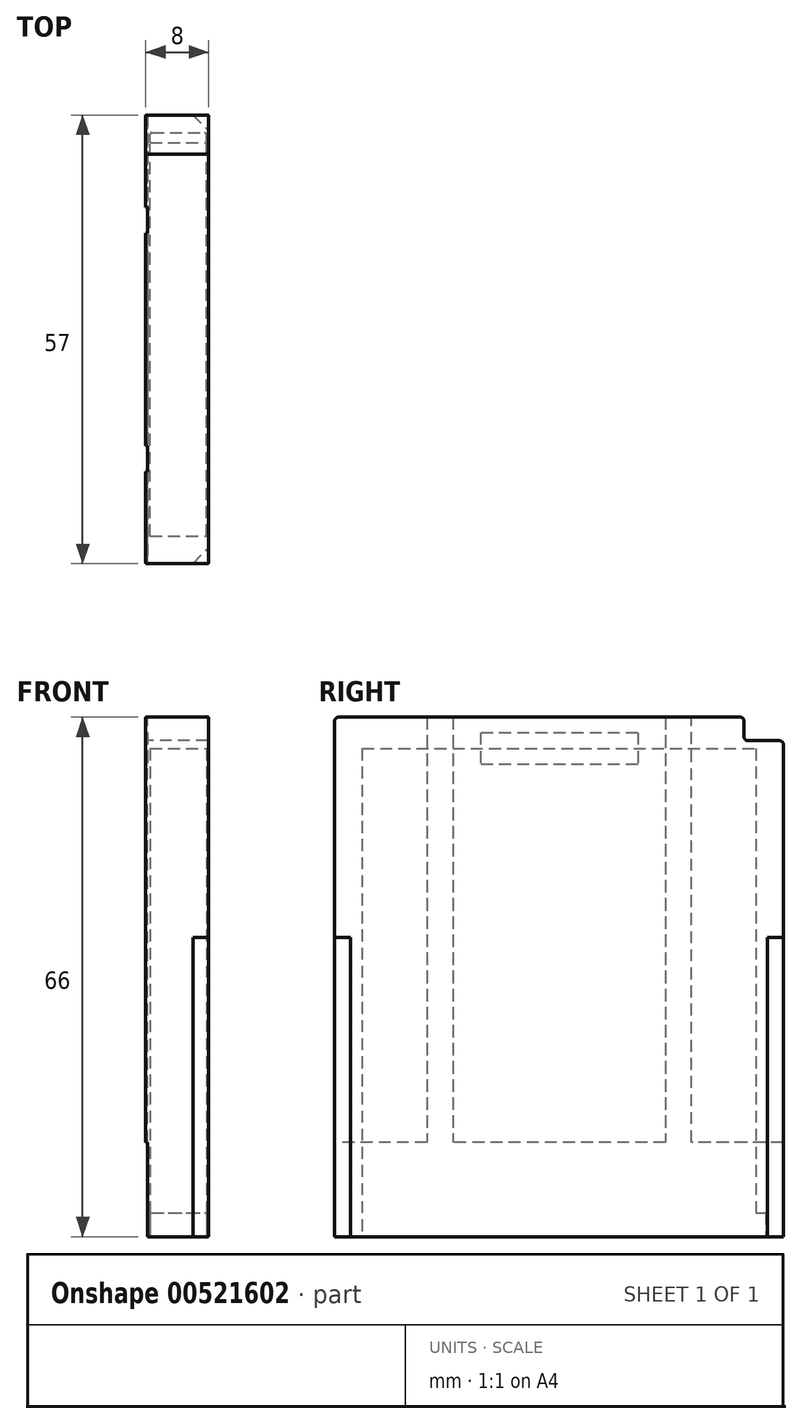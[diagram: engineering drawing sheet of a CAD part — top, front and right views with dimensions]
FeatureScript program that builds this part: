
annotation { "Feature Type Name" : "Feature", "Feature Type Description" : "" }
export const myFeature = defineFeature(function(context is Context, id is Id, definition is map)
    precondition{}
    {
        {
            var Q0;
            Q0=qCreatedBy(makeId("Right.planeOp"),FACE);
            var sketch = newSketch(context, id + "F0", { "sketchPlane" : qUnion([Q0])});
            skLineSegment(sketch, "E0.bottom", {"start": v(-28.5, 33) * mm, "end": v(23.5, 33) * mm});
            skLineSegment(sketch, "E0.top", {"start": v(-28.5, -33) * mm, "end": v(28.5, -33) * mm});
            skLineSegment(sketch, "E0.left", {"start": v(-28.5, 33) * mm, "end": v(-28.5, -33) * mm});
            skLineSegment(sketch, "E0.right", {"start": v(28.5, 30) * mm, "end": v(28.5, -33) * mm});
            skPoint(sketch, "E0.middle", {"position": v(0, 0) * mm});
            skLineSegment(sketch, "E1", {"start": v(23.5, 33) * mm, "end": v(23.5, 30) * mm});
            skLineSegment(sketch, "E2", {"start": v(23.5, 30) * mm, "end": v(28.5, 30) * mm});
            skSolve(sketch);
        }
        {
            var Q0;
            Q0=makeQuery(id+"F0.imprint","IMPRINT",FACE,{"disambiguationData":[TD([[makeQuery(id+"F0.imprint","IMPRINT",EDGE,{"derivedFrom":sQuery(id+"F0.wireOp",EDGE,"E0.bottom")}),-1.0]])]});
            extrude(context, id + "F1", {"entities" : qUnion([Q0]), "endBound" : BoundingType.SYMMETRIC, "depth" : 7.75 * mm, "offsetDistance" : 25 * mm});
        }
        {
            var Q0;
            Q0=makeQuery(id+"F1.opExtrude","SWEPT_FACE",FACE,{"disambiguationData":[OSD([sQuery(id+"F0.wireOp",EDGE,"E0.top")])]});
            var sketch = newSketch(context, id + "F2", { "sketchPlane" : qUnion([Q0])});
            skLineSegment(sketch, "E3", {"start": v(1.87, 28.5) * mm, "end": v(3.87, 26.5) * mm});
            skLineSegment(sketch, "E4", {"start": v(3.88, 26.5) * mm, "end": v(3.88, 28.5) * mm});
            skLineSegment(sketch, "E5", {"start": v(3.88, 28.5) * mm, "end": v(1.88, 28.5) * mm});
            skLineSegment(sketch, "E6", {"start": v(1.87, -28.5) * mm, "end": v(3.87, -26.5) * mm});
            skLineSegment(sketch, "E7", {"start": v(3.88, -26.5) * mm, "end": v(3.88, -28.5) * mm});
            skLineSegment(sketch, "E8", {"start": v(3.88, -28.5) * mm, "end": v(1.87, -28.5) * mm});
            skSolve(sketch);
        }
        {
            var Q0;
            Q0=qSketchRegion(id+"F2",true);
            extrude(context, id + "F3", {"entities" : qUnion([Q0]), "operationType" : NewBodyOperationType.REMOVE, "oppositeDirection" : true, "depth" : 38 * mm, "offsetDistance" : 25 * mm});
        }
        {
            var Q0;
            Q0=makeQuery(id+"F1.opExtrude","CAP_FACE",FACE,{"disambiguationData":[OSD([sQuery(id+"F0.wireOp",EDGE,"E0.bottom"),sQuery(id+"F0.wireOp",EDGE,"E0.top"),sQuery(id+"F0.wireOp",EDGE,"E0.left"),sQuery(id+"F0.wireOp",EDGE,"E0.right"),sQuery(id+"F0.wireOp",EDGE,"E1"),sQuery(id+"F0.wireOp",EDGE,"E2")])],"isStart":true});
            var sketch = newSketch(context, id + "F4", { "sketchPlane" : qUnion([Q0])});
            skLineSegment(sketch, "E9.bottom", {"start": v(-13.5, 33) * mm, "end": v(13.5, 33) * mm});
            skLineSegment(sketch, "E9.top", {"start": v(-13.5, -21) * mm, "end": v(13.5, -21) * mm});
            skLineSegment(sketch, "E9.left", {"start": v(-13.5, 33) * mm, "end": v(-13.5, -21) * mm});
            skLineSegment(sketch, "E9.right", {"start": v(13.5, 33) * mm, "end": v(13.5, -21) * mm});
            skLineSegment(sketch, "E10.bottom", {"start": v(16.8, 33) * mm, "end": v(28.5, 33) * mm});
            skLineSegment(sketch, "E10.top", {"start": v(16.8, -21) * mm, "end": v(28.5, -21) * mm});
            skLineSegment(sketch, "E10.left", {"start": v(16.8, 33) * mm, "end": v(16.8, -21) * mm});
            skLineSegment(sketch, "E10.right", {"start": v(28.5, 33) * mm, "end": v(28.5, -21) * mm});
            skLineSegment(sketch, "E11.bottom", {"start": v(-28.5, -21) * mm, "end": v(-16.8, -21) * mm});
            skLineSegment(sketch, "E11.top", {"start": v(-23.5, 33) * mm, "end": v(-16.8, 33) * mm});
            skLineSegment(sketch, "E11.left", {"start": v(-28.5, -21) * mm, "end": v(-28.5, 30) * mm});
            skLineSegment(sketch, "E11.right", {"start": v(-16.8, -21) * mm, "end": v(-16.8, 33) * mm});
            skLineSegment(sketch, "E12", {"start": v(-28.5, 30) * mm, "end": v(-23.5, 30) * mm});
            skLineSegment(sketch, "E13", {"start": v(-23.5, 30) * mm, "end": v(-23.5, 33) * mm});
            skLineSegment(sketch, "E14.bottom", {"start": v(-10, 31) * mm, "end": v(10, 31) * mm});
            skLineSegment(sketch, "E14.top", {"start": v(-10, 27) * mm, "end": v(10, 27) * mm});
            skLineSegment(sketch, "E14.left", {"start": v(-10, 31) * mm, "end": v(-10, 27) * mm});
            skLineSegment(sketch, "E14.right", {"start": v(10, 31) * mm, "end": v(10, 27) * mm});
            skSolve(sketch);
        }
        {
            var Q0;
            Q0=qSketchRegion(id+"F4",true);
            extrude(context, id + "F5", {"entities" : qUnion([Q0]), "operationType" : NewBodyOperationType.ADD, "depth" : .25 * mm, "offsetDistance" : 25 * mm});
        }
        {
            var Q0;
            Q0=makeQuery(id+"F1.opExtrude","CAP_FACE",FACE,{"disambiguationData":[OSD([sQuery(id+"F0.wireOp",EDGE,"E0.bottom"),sQuery(id+"F0.wireOp",EDGE,"E0.top"),sQuery(id+"F0.wireOp",EDGE,"E0.left"),sQuery(id+"F0.wireOp",EDGE,"E0.right"),sQuery(id+"F0.wireOp",EDGE,"E1"),sQuery(id+"F0.wireOp",EDGE,"E2")])],"isStart":false});
            var sketch = newSketch(context, id + "F6", { "sketchPlane" : qUnion([Q0])});
            skLineSegment(sketch, "E15.bottom", {"start": v(-16, 29) * mm, "end": v(16, 29) * mm});
            skLineSegment(sketch, "E15.top", {"start": v(-16, 17) * mm, "end": v(16, 17) * mm});
            skPoint(sketch, "E15.middle", {"position": v(0, 23) * mm});
            skArc(sketch, "E16", {"start": v(16, 17) * mm, "mid": v(22, 23) * mm, "end": v(16, 29) * mm});
            skArc(sketch, "E17", {"start": v(-16, 29) * mm, "mid": v(-22, 23) * mm, "end": v(-16, 17) * mm});
            skSolve(sketch);
        }
        {
            var Q0;
            Q0=makeQuery(id+"F1.opExtrude","CAP_FACE",FACE,{"disambiguationData":[OSD([sQuery(id+"F0.wireOp",EDGE,"E0.bottom"),sQuery(id+"F0.wireOp",EDGE,"E0.top"),sQuery(id+"F0.wireOp",EDGE,"E0.left"),sQuery(id+"F0.wireOp",EDGE,"E0.right"),sQuery(id+"F0.wireOp",EDGE,"E1"),sQuery(id+"F0.wireOp",EDGE,"E2")])],"isStart":false});
            var sketch = newSketch(context, id + "F7", { "sketchPlane" : qUnion([Q0])});
            skArc(sketch, "E18", {"start": v(20.7, 18.5) * mm, "mid": v(21.1, 18.98) * mm, "end": v(21.48, 19.5) * mm});
            skLineSegment(sketch, "E19", {"start": v(20.7, 27.5) * mm, "end": v(28.5, 27.5) * mm});
            skLineSegment(sketch, "E20", {"start": v(28.5, 27.5) * mm, "end": v(28.5, 26.5) * mm});
            skLineSegment(sketch, "E21", {"start": v(28.5, 26.5) * mm, "end": v(21.48, 26.5) * mm});
            skLineSegment(sketch, "E22", {"start": v(22, 25.5) * mm, "end": v(28.5, 25.5) * mm});
            skLineSegment(sketch, "E23", {"start": v(28.5, 25.5) * mm, "end": v(28.5, 24.5) * mm});
            skLineSegment(sketch, "E24", {"start": v(28.5, 24.5) * mm, "end": v(22.32, 24.5) * mm});
            skLineSegment(sketch, "E25", {"start": v(22.48, 23.5) * mm, "end": v(28.5, 23.5) * mm});
            skLineSegment(sketch, "E26", {"start": v(28.5, 23.5) * mm, "end": v(28.5, 22.5) * mm});
            skLineSegment(sketch, "E27", {"start": v(28.5, 22.5) * mm, "end": v(22.48, 22.5) * mm});
            skLineSegment(sketch, "E28", {"start": v(22.32, 21.5) * mm, "end": v(28.5, 21.5) * mm});
            skLineSegment(sketch, "E29", {"start": v(21.48, 19.5) * mm, "end": v(28.5, 19.5) * mm});
            skLineSegment(sketch, "E30", {"start": v(28.5, 21.5) * mm, "end": v(28.5, 20.5) * mm});
            skLineSegment(sketch, "E31", {"start": v(28.5, 20.5) * mm, "end": v(22, 20.5) * mm});
            skLineSegment(sketch, "E32", {"start": v(28.5, 19.5) * mm, "end": v(28.5, 18.5) * mm});
            skLineSegment(sketch, "E33", {"start": v(28.5, 18.5) * mm, "end": v(20.7, 18.5) * mm});
            skArc(sketch, "E34.trimOffspring", {"start": v(21.48, 26.5) * mm, "mid": v(21.1, 27.02) * mm, "end": v(20.7, 27.5) * mm});
            skArc(sketch, "E35.trimOffspring", {"start": v(22.32, 24.5) * mm, "mid": v(22.18, 25) * mm, "end": v(22, 25.5) * mm});
            skArc(sketch, "E36.trimOffspring", {"start": v(22.48, 22.5) * mm, "mid": v(22.5, 23) * mm, "end": v(22.48, 23.5) * mm});
            skArc(sketch, "E37.trimOffspring", {"start": v(22, 20.5) * mm, "mid": v(22.18, 21) * mm, "end": v(22.32, 21.5) * mm});
            skArc(sketch, "E38.MirrorCS", {"start": v(-22.48, 22.5) * mm, "mid": v(-22.5, 23) * mm, "end": v(-22.48, 23.5) * mm});
            skLineSegment(sketch, "E39.MirrorCS", {"start": v(-28.5, 23.5) * mm, "end": v(-28.5, 22.5) * mm});
            skLineSegment(sketch, "E40.MirrorCS", {"start": v(-28.5, 21.5) * mm, "end": v(-28.5, 20.5) * mm});
            skArc(sketch, "E41.MirrorCS", {"start": v(-22, 20.5) * mm, "mid": v(-22.18, 21) * mm, "end": v(-22.32, 21.5) * mm});
            skArc(sketch, "E42.MirrorCS", {"start": v(-22.32, 24.5) * mm, "mid": v(-22.18, 25) * mm, "end": v(-22, 25.5) * mm});
            skLineSegment(sketch, "E43.MirrorCS", {"start": v(-28.5, 19.5) * mm, "end": v(-28.5, 18.5) * mm});
            skLineSegment(sketch, "E44.MirrorCS", {"start": v(-28.5, 25.5) * mm, "end": v(-28.5, 24.5) * mm});
            skLineSegment(sketch, "E45.MirrorCS", {"start": v(-28.5, 27.5) * mm, "end": v(-28.5, 26.5) * mm});
            skArc(sketch, "E46.MirrorCS", {"start": v(-21.48, 26.5) * mm, "mid": v(-21.1, 27.02) * mm, "end": v(-20.7, 27.5) * mm});
            skArc(sketch, "E47.MirrorCS", {"start": v(-20.7, 18.5) * mm, "mid": v(-21.1, 18.98) * mm, "end": v(-21.48, 19.5) * mm});
            skLineSegment(sketch, "E48.MirrorCS", {"start": v(-28.5, 18.5) * mm, "end": v(-20.7, 18.5) * mm});
            skLineSegment(sketch, "E49.MirrorCS", {"start": v(-20.7, 27.5) * mm, "end": v(-28.5, 27.5) * mm});
            skLineSegment(sketch, "E50.MirrorCS", {"start": v(-28.5, 26.5) * mm, "end": v(-21.48, 26.5) * mm});
            skLineSegment(sketch, "E51.MirrorCS", {"start": v(-22, 25.5) * mm, "end": v(-28.5, 25.5) * mm});
            skLineSegment(sketch, "E52.MirrorCS", {"start": v(-28.5, 24.5) * mm, "end": v(-22.32, 24.5) * mm});
            skLineSegment(sketch, "E53.MirrorCS", {"start": v(-22.48, 23.5) * mm, "end": v(-28.5, 23.5) * mm});
            skLineSegment(sketch, "E54.MirrorCS", {"start": v(-21.48, 19.5) * mm, "end": v(-28.5, 19.5) * mm});
            skLineSegment(sketch, "E55.MirrorCS", {"start": v(-28.5, 20.5) * mm, "end": v(-22, 20.5) * mm});
            skLineSegment(sketch, "E56.MirrorCS", {"start": v(-22.32, 21.5) * mm, "end": v(-28.5, 21.5) * mm});
            skLineSegment(sketch, "E57.MirrorCS", {"start": v(-28.5, 22.5) * mm, "end": v(-22.48, 22.5) * mm});
            skSolve(sketch);
        }
        {
            var Q0;
            Q0=makeQuery(id+"F5.boolean.opBoolean","MERGE",EDGE,{"derivedFrom":[makeQuery(id+"F1.opExtrude","SWEPT_EDGE",EDGE,{"disambiguationData":[OSD([sQuery(id+"F0.wireOp",EDGE,"E0.bottom"),sQuery(id+"F0.wireOp",EDGE,"E1")])]}),makeQuery(id+"F5.opExtrude","SWEPT_EDGE",EDGE,{"disambiguationData":[OSD([sQuery(id+"F4.wireOp",EDGE,"E11.top"),sQuery(id+"F4.wireOp",EDGE,"E13")])]})]});
            var Q1;
            Q1=makeQuery(id+"F5.boolean.opBoolean","MERGE",EDGE,{"derivedFrom":[makeQuery(id+"F1.opExtrude","SWEPT_EDGE",EDGE,{"disambiguationData":[OSD([sQuery(id+"F0.wireOp",EDGE,"E1"),sQuery(id+"F0.wireOp",EDGE,"E2")])]}),makeQuery(id+"F5.opExtrude","SWEPT_EDGE",EDGE,{"disambiguationData":[OSD([sQuery(id+"F4.wireOp",EDGE,"E12"),sQuery(id+"F4.wireOp",EDGE,"E13")])]})]});
            var Q2;
            Q2=makeQuery(id+"F5.boolean.opBoolean","MERGE",EDGE,{"derivedFrom":[makeQuery(id+"F1.opExtrude","SWEPT_EDGE",EDGE,{"disambiguationData":[OSD([sQuery(id+"F0.wireOp",EDGE,"E0.right"),sQuery(id+"F0.wireOp",EDGE,"E2")])]}),makeQuery(id+"F5.opExtrude","SWEPT_EDGE",EDGE,{"disambiguationData":[OSD([sQuery(id+"F4.wireOp",EDGE,"E11.left"),sQuery(id+"F4.wireOp",EDGE,"E12")])]})]});
            var Q3;
            Q3=makeQuery(id+"F5.boolean.opBoolean","MERGE",EDGE,{"derivedFrom":[makeQuery(id+"F1.opExtrude","SWEPT_EDGE",EDGE,{"disambiguationData":[OSD([sQuery(id+"F0.wireOp",EDGE,"E0.bottom"),sQuery(id+"F0.wireOp",EDGE,"E0.left")])]}),makeQuery(id+"F5.opExtrude","SWEPT_EDGE",EDGE,{"disambiguationData":[OSD([sQuery(id+"F4.wireOp",EDGE,"E10.bottom"),sQuery(id+"F4.wireOp",EDGE,"E10.right")])]})]});
            fillet(context, id + "F8", {"entities" : qUnion([Q0, Q1, Q2, Q3]), "radius" : .5 * mm, "tangentPropagation" : true, "allowEdgeOverflow" : false});
        }
        {
            var Q0;
            Q0=makeQuery(id+"F1.opExtrude","CAP_EDGE",EDGE,{"disambiguationData":[OSD([sQuery(id+"F0.wireOp",EDGE,"E0.bottom")])],"isStart":false});
            var Q1;
            Q1=makeQuery(id+"F1.opExtrude","CAP_EDGE",EDGE,{"disambiguationData":[OSD([sQuery(id+"F0.wireOp",EDGE,"E2")])],"isStart":false});
            var Q2;
            Q2=makeQuery(id+"F5.opExtrude","CAP_EDGE",EDGE,{"disambiguationData":[OSD([sQuery(id+"F4.wireOp",EDGE,"E12")])],"isStart":false});
            var Q3;
            Q3=makeQuery(id+"F5.opExtrude","CAP_EDGE",EDGE,{"disambiguationData":[OSD([sQuery(id+"F4.wireOp",EDGE,"E13")])],"isStart":false});
            var Q4;
            Q4=makeQuery(id+"F1.opExtrude","CAP_EDGE",EDGE,{"disambiguationData":[OSD([sQuery(id+"F0.wireOp",EDGE,"E1")])],"isStart":false});
            var Q5;
            Q5=makeQuery(id+"F5.opExtrude","CAP_EDGE",EDGE,{"disambiguationData":[OSD([sQuery(id+"F4.wireOp",EDGE,"E11.top")])],"isStart":false});
            var Q6;
            Q6=makeQuery(id+"F5.opExtrude","CAP_EDGE",EDGE,{"disambiguationData":[OSD([sQuery(id+"F4.wireOp",EDGE,"E9.bottom")])],"isStart":false});
            var Q7;
            Q7=makeQuery(id+"F5.opExtrude","CAP_EDGE",EDGE,{"disambiguationData":[OSD([sQuery(id+"F4.wireOp",EDGE,"E10.bottom")])],"isStart":false});
            var Q8;
            {var subQ0=sQuery(id+"F4.wireOp",EDGE,"E10.right");Q8=makeQuery(id+"FrGKLvruxDWx0Zx_1.1.FIEsVdhnxNMygbw_1.boolean.opBoolean","SPLIT",EDGE,{"disambiguationData":[TD([makeQuery(id+"F1.opExtrude","SWEPT_FACE",FACE,{"disambiguationData":[OSD([sQuery(id+"F0.wireOp",EDGE,"E0.bottom")])]})])],"derivedFrom":makeQuery(id+"F5.opExtrude","CAP_EDGE",EDGE,{"disambiguationData":[OSD([subQ0])],"isStart":false})});}
            var Q9;
            {var subQ0=sQuery(id+"F0.wireOp",EDGE,"E0.left");var subQ1=sQuery(id+"F0.wireOp",EDGE,"E0.bottom");Q9=makeQuery(id+"FVF8a06UCtymIsE_1.boolean.opBoolean","SPLIT",EDGE,{"disambiguationData":[TD([makeQuery(id+"F1.opExtrude","SWEPT_FACE",FACE,{"disambiguationData":[OSD([subQ1])]})])],"derivedFrom":makeQuery(id+"F1.opExtrude","CAP_EDGE",EDGE,{"disambiguationData":[OSD([subQ0])],"isStart":false})});}
            var Q10;
            {var subQ0=sQuery(id+"F0.wireOp",EDGE,"E0.left");Q10=makeQuery(id+"FVF8a06UCtymIsE_1.boolean.opBoolean","SPLIT",EDGE,{"disambiguationData":[TD([makeQuery(id+"FVF8a06UCtymIsE_1.opExtrude","SWEPT_FACE",FACE,{"disambiguationData":[OSD([sQuery(id+"F7.wireOp",EDGE,"E48.MirrorCS")])]})])],"derivedFrom":makeQuery(id+"F1.opExtrude","CAP_EDGE",EDGE,{"disambiguationData":[OSD([subQ0])],"isStart":false})});}
            var Q11;
            {var subQ0=sQuery(id+"F4.wireOp",EDGE,"E10.top");var subQ1=sQuery(id+"F4.wireOp",EDGE,"E10.right");Q11=makeQuery(id+"FrGKLvruxDWx0Zx_1.1.FIEsVdhnxNMygbw_1.boolean.opBoolean","SPLIT",EDGE,{"disambiguationData":[TD([makeQuery(id+"F5.opExtrude","SWEPT_FACE",FACE,{"disambiguationData":[OSD([subQ0])]})])],"derivedFrom":makeQuery(id+"F5.opExtrude","CAP_EDGE",EDGE,{"disambiguationData":[OSD([subQ1])],"isStart":false})});}
            var Q12;
            {var subQ0=sQuery(id+"F0.wireOp",EDGE,"E0.right");Q12=makeQuery(id+"FVF8a06UCtymIsE_1.boolean.opBoolean","SPLIT",EDGE,{"disambiguationData":[TD([makeQuery(id+"FVF8a06UCtymIsE_1.opExtrude","SWEPT_FACE",FACE,{"disambiguationData":[OSD([sQuery(id+"F7.wireOp",EDGE,"E33")])]})])],"derivedFrom":makeQuery(id+"F1.opExtrude","CAP_EDGE",EDGE,{"disambiguationData":[OSD([subQ0])],"isStart":false})});}
            var Q13;
            {var subQ0=sQuery(id+"F4.wireOp",EDGE,"E11.left");var subQ1=sQuery(id+"F4.wireOp",EDGE,"E11.bottom");Q13=makeQuery(id+"FIEsVdhnxNMygbw_1.boolean.opBoolean","SPLIT",EDGE,{"disambiguationData":[TD([makeQuery(id+"F5.opExtrude","SWEPT_FACE",FACE,{"disambiguationData":[OSD([subQ1])]})])],"derivedFrom":makeQuery(id+"F5.opExtrude","CAP_EDGE",EDGE,{"disambiguationData":[OSD([subQ0])],"isStart":false})});}
            fillet(context, id + "F9", {"entities" : qUnion([Q0, Q1, Q2, Q3, Q4, Q5, Q6, Q7, Q8, Q9, Q10, Q11, Q12, Q13]), "radius" : .1 * mm, "tangentPropagation" : true, "allowEdgeOverflow" : false});
        }
        {
            var Q0;
            Q0=makeQuery(id+"F1.opExtrude","CAP_FACE",FACE,{"disambiguationData":[OSD([sQuery(id+"F0.wireOp",EDGE,"E0.bottom"),sQuery(id+"F0.wireOp",EDGE,"E0.top"),sQuery(id+"F0.wireOp",EDGE,"E0.left"),sQuery(id+"F0.wireOp",EDGE,"E0.right"),sQuery(id+"F0.wireOp",EDGE,"E1"),sQuery(id+"F0.wireOp",EDGE,"E2")])],"isStart":false});
            var sketch = newSketch(context, id + "F10", { "sketchPlane" : qUnion([Q0])});
            skLineSegment(sketch, "E58.bottom", {"start": v(-21.75, 14.25) * mm, "end": v(21.75, 14.25) * mm});
            skLineSegment(sketch, "E58.top", {"start": v(-21.75, -25.25) * mm, "end": v(21.75, -25.25) * mm});
            skLineSegment(sketch, "E58.left", {"start": v(-22, 14) * mm, "end": v(-22, -25) * mm});
            skLineSegment(sketch, "E58.right", {"start": v(22, 14) * mm, "end": v(22, -25) * mm});
            skPoint(sketch, "E58.middle", {"position": v(0, -5.5) * mm});
            skLineSegment(sketch, "E59", {"start": v(-3.94, -26.55) * mm, "end": v(3.94, -26.55) * mm});
            skLineSegment(sketch, "E60", {"start": v(4.12, -26.97) * mm, "end": v(0.19, -31.34) * mm});
            skLineSegment(sketch, "E61", {"start": v(-0.19, -31.34) * mm, "end": v(-4.12, -26.97) * mm});
            skPoint(sketch, "E62.visualSharp", {"position": v(-22, 14.25) * mm});
            skArc(sketch, "E62.filletArc", {"start": v(-21.75, 14.25) * mm, "mid": v(-21.93, 14.18) * mm, "end": v(-22, 14) * mm});
            skPoint(sketch, "E63.visualSharp", {"position": v(22, 14.25) * mm});
            skArc(sketch, "E63.filletArc", {"start": v(22, 14) * mm, "mid": v(21.93, 14.18) * mm, "end": v(21.75, 14.25) * mm});
            skPoint(sketch, "E64.visualSharp", {"position": v(-22, -25.25) * mm});
            skArc(sketch, "E64.filletArc", {"start": v(-22, -25) * mm, "mid": v(-21.93, -25.18) * mm, "end": v(-21.75, -25.25) * mm});
            skPoint(sketch, "E65.visualSharp", {"position": v(22, -25.25) * mm});
            skArc(sketch, "E65.filletArc", {"start": v(21.75, -25.25) * mm, "mid": v(21.93, -25.18) * mm, "end": v(22, -25) * mm});
            skPoint(sketch, "E66.visualSharp", {"position": v(-4.5, -26.55) * mm});
            skArc(sketch, "E66.filletArc", {"start": v(-3.94, -26.55) * mm, "mid": v(-4.17, -26.7) * mm, "end": v(-4.12, -26.97) * mm});
            skPoint(sketch, "E67.visualSharp", {"position": v(4.5, -26.55) * mm});
            skArc(sketch, "E67.filletArc", {"start": v(4.12, -26.97) * mm, "mid": v(4.17, -26.7) * mm, "end": v(3.94, -26.55) * mm});
            skPoint(sketch, "E68.visualSharp", {"position": v(0, -31.55) * mm});
            skArc(sketch, "E68.filletArc", {"start": v(-0.19, -31.34) * mm, "mid": v(0, -31.43) * mm, "end": v(0.19, -31.34) * mm});
            skSolve(sketch);
        }
        {
            var Q0;
            Q0=makeQuery(id+"F1.opExtrude","SWEPT_FACE",FACE,{"disambiguationData":[OSD([sQuery(id+"F0.wireOp",EDGE,"E0.top")])]});
            var sketch = newSketch(context, id + "F11", { "sketchPlane" : qUnion([Q0])});
            skLineSegment(sketch, "E69.bottom", {"start": v(-3.57, 25) * mm, "end": v(3.58, 25) * mm});
            skLineSegment(sketch, "E69.top", {"start": v(-3.58, -25) * mm, "end": v(3.57, -25) * mm});
            skLineSegment(sketch, "E69.left", {"start": v(-3.57, 25) * mm, "end": v(-3.58, -25) * mm});
            skLineSegment(sketch, "E69.right", {"start": v(3.58, 25) * mm, "end": v(3.57, -25) * mm});
            skPoint(sketch, "E69.middle", {"position": v(0, 0) * mm});
            skSolve(sketch);
        }
        {
            var Q0;
            Q0=makeQuery(id+"F11.imprint","IMPRINT",FACE,{"disambiguationData":[TD([[makeQuery(id+"F11.imprint","IMPRINT",EDGE,{"derivedFrom":sQuery(id+"F11.wireOp",EDGE,"E69.bottom")}),-1.0]])]});
            extrude(context, id + "F12", {"entities" : qUnion([Q0]), "operationType" : NewBodyOperationType.REMOVE, "oppositeDirection" : true, "depth" : 62 * mm, "offsetDistance" : 25 * mm});
        }
        {
            var Q0;
            Q0=makeQuery(id+"F1.opExtrude","SWEPT_FACE",FACE,{"disambiguationData":[OSD([sQuery(id+"F0.wireOp",EDGE,"E0.top")])]});
            var sketch = newSketch(context, id + "F13", { "sketchPlane" : qUnion([Q0])});
            skLineSegment(sketch, "E70.bottom", {"start": v(-3.58, -25) * mm, "end": v(3.57, -25) * mm});
            skLineSegment(sketch, "E70.top", {"start": v(-3.33, -26.25) * mm, "end": v(3.32, -26.25) * mm});
            skLineSegment(sketch, "E70.left", {"start": v(-3.58, -25) * mm, "end": v(-3.58, -26) * mm});
            skLineSegment(sketch, "E70.right", {"start": v(3.57, -25) * mm, "end": v(3.57, -26) * mm});
            skPoint(sketch, "E71.visualSharp", {"position": v(-3.58, -26.25) * mm});
            skArc(sketch, "E71.filletArc", {"start": v(-3.58, -26) * mm, "mid": v(-3.5, -26.18) * mm, "end": v(-3.33, -26.25) * mm});
            skPoint(sketch, "E72.visualSharp", {"position": v(3.57, -26.25) * mm});
            skArc(sketch, "E72.filletArc", {"start": v(3.32, -26.25) * mm, "mid": v(3.5, -26.18) * mm, "end": v(3.58, -26) * mm});
            skSolve(sketch);
        }
        {
            var Q0;
            Q0=qSketchRegion(id+"F13",true);
            extrude(context, id + "F14", {"entities" : qUnion([Q0]), "operationType" : NewBodyOperationType.REMOVE, "oppositeDirection" : true, "depth" : 3 * mm, "offsetDistance" : 25 * mm});
        }
    });
